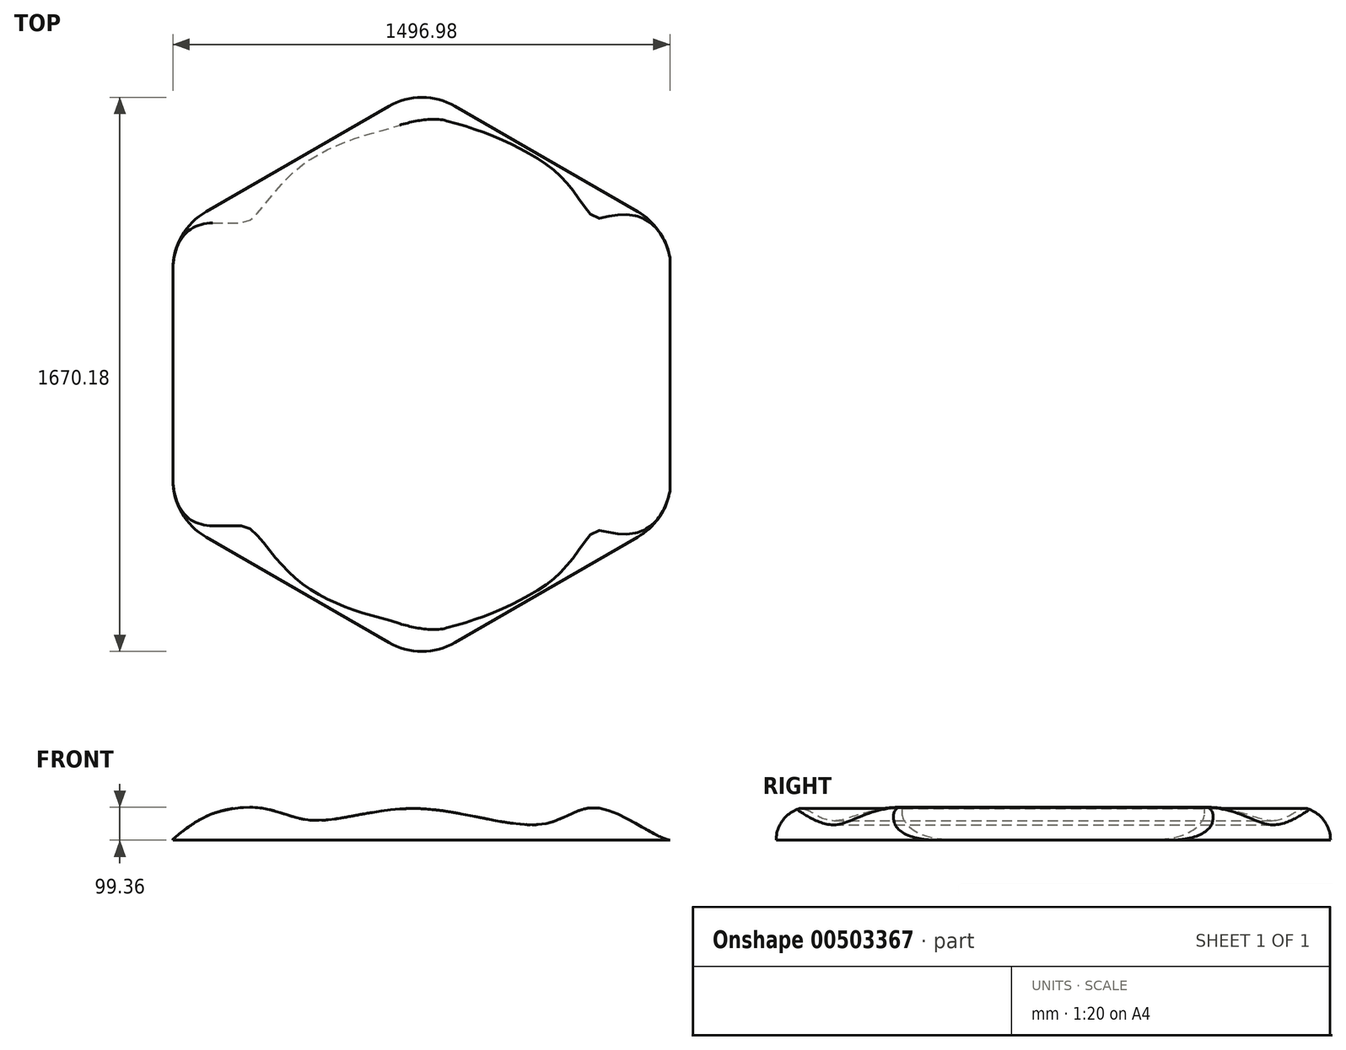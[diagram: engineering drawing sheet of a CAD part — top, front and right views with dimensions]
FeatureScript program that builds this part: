
annotation { "Feature Type Name" : "Feature", "Feature Type Description" : "" }
export const myFeature = defineFeature(function(context is Context, id is Id, definition is map)
    precondition{}
    {
        {
            var Q0;
            Q0=qCreatedBy(makeId("Top.planeOp"),FACE);
            var sketch = newSketch(context, id + "F0", { "sketchPlane" : qUnion([Q0])});
            skCircle(sketch, "E0.cCircle", {"center": v(0, 0) * mm, "radius": 750 * mm, "construction": true});
            skLineSegment(sketch, "E0.0", {"start": v(750, 433.01) * mm, "end": v(750, -433.01) * mm});
            skLineSegment(sketch, "E0.1", {"start": v(750, -433.01) * mm, "end": v(0, -866.03) * mm});
            skLineSegment(sketch, "E0.2", {"start": v(0, -866.03) * mm, "end": v(-750, -433.01) * mm});
            skLineSegment(sketch, "E0.3", {"start": v(-750, -433.01) * mm, "end": v(-750, 433.01) * mm});
            skLineSegment(sketch, "E0.4", {"start": v(-750, 433.01) * mm, "end": v(0, 866.03) * mm});
            skLineSegment(sketch, "E0.5", {"start": v(0, 866.03) * mm, "end": v(750, 433.01) * mm});
            skPoint(sketch, "E0.0.midPoint", {"position": v(750, 0) * mm});
            skSolve(sketch);
        }
        {
            var Q0;
            Q0=makeQuery(id+"F0.imprint","IMPRINT",FACE,{"disambiguationData":[TD([[makeQuery(id+"F0.imprint","IMPRINT",EDGE,{"derivedFrom":sQuery(id+"F0.wireOp",EDGE,"E0.0")}),-1.0]])]});
            extrude(context, id + "F1", {"entities" : qUnion([Q0]), "depth" : 100 * mm});
        }
        {
            var Q0;
            Q0=makeQuery(id+"F1.opExtrude","SWEPT_EDGE",EDGE,{"disambiguationData":[OSD([sQuery(id+"F0.wireOp",EDGE,"E0.1"),sQuery(id+"F0.wireOp",EDGE,"E0.2")])]});
            var Q1;
            Q1=makeQuery(id+"F1.opExtrude","SWEPT_EDGE",EDGE,{"disambiguationData":[OSD([sQuery(id+"F0.wireOp",EDGE,"E0.0"),sQuery(id+"F0.wireOp",EDGE,"E0.1")])]});
            var Q2;
            Q2=makeQuery(id+"F1.opExtrude","SWEPT_EDGE",EDGE,{"disambiguationData":[OSD([sQuery(id+"F0.wireOp",EDGE,"E0.0"),sQuery(id+"F0.wireOp",EDGE,"E0.5")])]});
            var Q3;
            Q3=makeQuery(id+"F1.opExtrude","SWEPT_EDGE",EDGE,{"disambiguationData":[OSD([sQuery(id+"F0.wireOp",EDGE,"E0.4"),sQuery(id+"F0.wireOp",EDGE,"E0.5")])]});
            var Q4;
            Q4=makeQuery(id+"F1.opExtrude","SWEPT_EDGE",EDGE,{"disambiguationData":[OSD([sQuery(id+"F0.wireOp",EDGE,"E0.2"),sQuery(id+"F0.wireOp",EDGE,"E0.3")])]});
            var Q5;
            Q5=makeQuery(id+"F1.opExtrude","SWEPT_EDGE",EDGE,{"disambiguationData":[OSD([sQuery(id+"F0.wireOp",EDGE,"E0.3"),sQuery(id+"F0.wireOp",EDGE,"E0.4")])]});
            fillet(context, id + "F2", {"entities" : qUnion([Q0, Q1, Q2, Q3, Q4, Q5]), "radius" : 200 * mm, "tangentPropagation" : true, "allowEdgeOverflow" : false});
        }
        {
            var Q0;
            Q0=makeQuery(id+"F1.opExtrude","CAP_FACE",FACE,{"disambiguationData":[OSD([sQuery(id+"F0.wireOp",EDGE,"E0.0"),sQuery(id+"F0.wireOp",EDGE,"E0.1"),sQuery(id+"F0.wireOp",EDGE,"E0.2"),sQuery(id+"F0.wireOp",EDGE,"E0.3"),sQuery(id+"F0.wireOp",EDGE,"E0.4"),sQuery(id+"F0.wireOp",EDGE,"E0.5")])],"isStart":false});
            fillet(context, id + "F3", {"entities" : qUnion([Q0]), "radius" : 100 * mm, "tangentPropagation" : true, "allowEdgeOverflow" : false});
        }
        {
            var Q0;
            Q0=qCreatedBy(makeId("Front.planeOp"),FACE);
            var sketch = newSketch(context, id + "F4", { "sketchPlane" : qUnion([Q0])});
            skFitSpline(sketch, "E1", {"points": [v(-753.62, 0) * mm, v(-637.33, 77.06) * mm, v(-473.42, 95.37) * mm, v(-326.9, 59.66) * mm, v(-11.9, 95.37) * mm, v(369.94, 49.59) * mm, v(538.43, 96.29) * mm, v(760.03, 0) * mm, v(756.37, 148.48) * mm], "startDerivative": vector(1033.7, 856.81) * mm, "endDerivative": vector(-458.82, 2000.07) * mm});
            skLineSegment(sketch, "E2", {"start": v(-753.62, 0) * mm, "end": v(-753.62, 173.2) * mm});
            skLineSegment(sketch, "E3", {"start": v(-753.62, 173.2) * mm, "end": v(756.37, 148.48) * mm});
            skSolve(sketch);
        }
        {
            var Q0;
            Q0=makeQuery(id+"F4.imprint","IMPRINT",FACE,{"disambiguationData":[TD([[makeQuery(id+"F4.imprint","IMPRINT",EDGE,{"derivedFrom":sQuery(id+"F4.wireOp",EDGE,"E1")}),1.0]])]});
            extrude(context, id + "F5", {"entities" : qUnion([Q0]), "operationType" : NewBodyOperationType.REMOVE, "depth" : 1500 * mm, "hasSecondDirection" : true, "secondDirectionOppositeDirection" : true, "secondDirectionDepth" : 1500 * mm});
        }
    });
